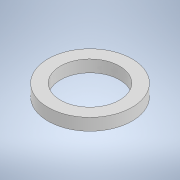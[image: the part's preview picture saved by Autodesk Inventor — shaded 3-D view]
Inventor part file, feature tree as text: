
AUTODESK INVENTOR PART (.ipt)
format: ipt  version: 2022 (Build 260153000, 153)  size: 99,328 bytes
history: native  units: in
note: dims shown in document units (in); Inventor stores cm internally (conversion verified against a paired STEP export)
features: extrude x1, sketch x1
ambient origin geometry x8: Origin, YZ Plane, XZ Plane, XY Plane, X Axis, Y Axis, Z Axis, Center Point
bodies: Solid1 (feature_tree)
feature tree (2):
  extrude  "Extrusion1"  Depth=0.1in
  sketch  "Sketch1"  dims[d0=0.4921in d1=0.7in d2=0.1in d3=0.0in]
